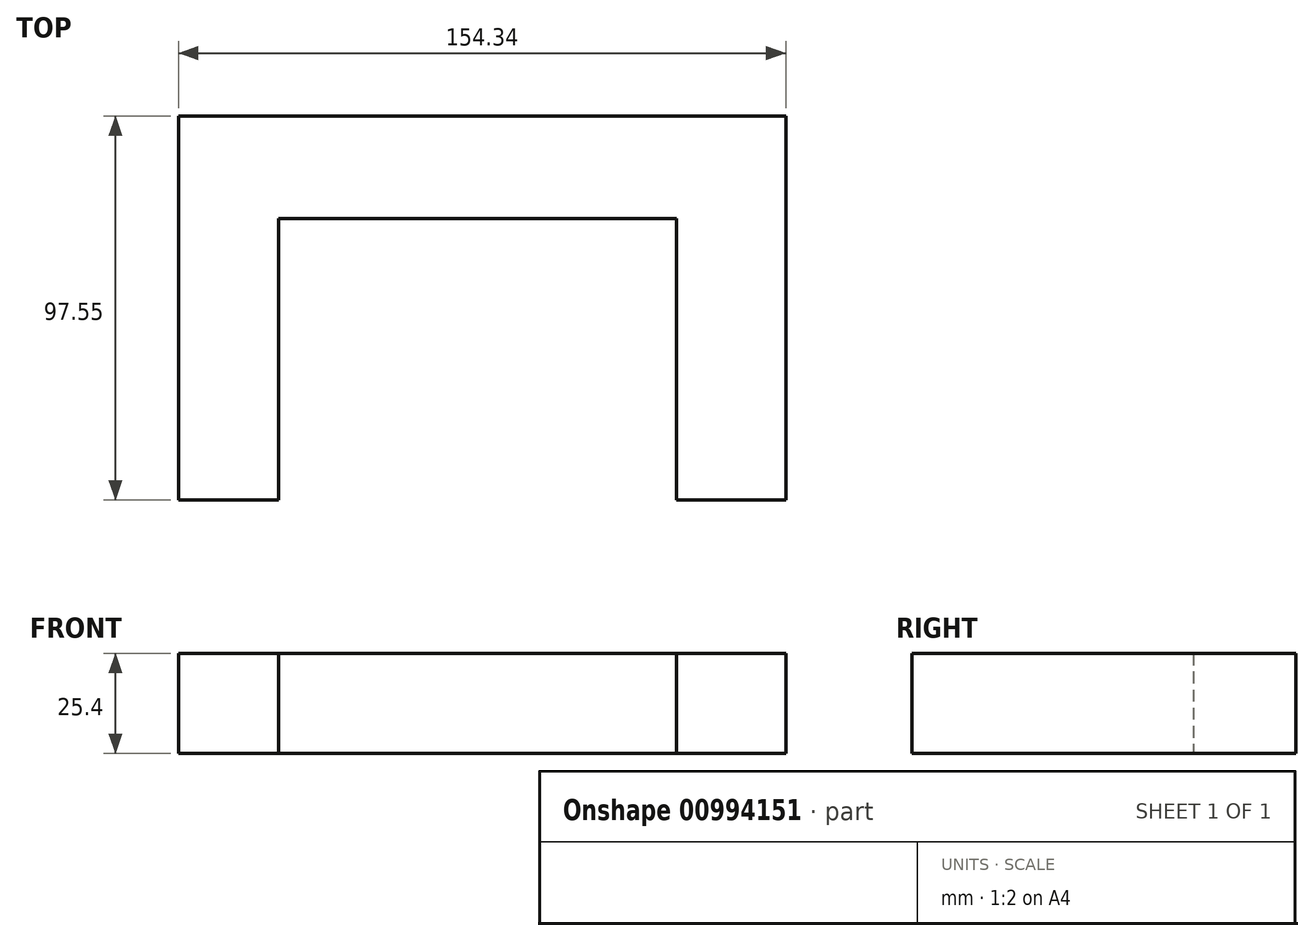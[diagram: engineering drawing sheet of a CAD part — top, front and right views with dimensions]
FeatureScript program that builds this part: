
annotation { "Feature Type Name" : "Feature", "Feature Type Description" : "" }
export const myFeature = defineFeature(function(context is Context, id is Id, definition is map)
    precondition{}
    {
        {
            var Q0;
            Q0=qCreatedBy(makeId("Top.planeOp"),FACE);
            var sketch = newSketch(context, id + "F0", { "sketchPlane" : qUnion([Q0])});
            skLineSegment(sketch, "E0.bottom", {"start": v(86.83, 58.57) * mm, "end": v(-67.5, 58.57) * mm});
            skLineSegment(sketch, "E0.top", {"start": v(86.83, -38.98) * mm, "end": v(-67.5, -38.98) * mm});
            skLineSegment(sketch, "E0.left", {"start": v(86.83, 58.57) * mm, "end": v(86.83, -38.98) * mm});
            skLineSegment(sketch, "E0.right", {"start": v(-67.5, 58.57) * mm, "end": v(-67.5, -38.98) * mm});
            skLineSegment(sketch, "E1", {"start": v(-42.07, 17.04) * mm, "end": v(-42.07, -38.98) * mm});
            skLineSegment(sketch, "E2", {"start": v(-42.07, -38.98) * mm, "end": v(-42.07, 32.56) * mm});
            skLineSegment(sketch, "E3", {"start": v(-42.07, 32.56) * mm, "end": v(59.07, 32.56) * mm});
            skLineSegment(sketch, "E4", {"start": v(59.07, 32.56) * mm, "end": v(59.07, -38.98) * mm});
            skSolve(sketch);
        }
        {
            var Q0;
            Q0=makeQuery(id+"F0.imprint","IMPRINT",FACE,{"disambiguationData":[TD([[makeQuery(id+"F0.imprint","IMPRINT",EDGE,{"derivedFrom":sQuery(id+"F0.wireOp",EDGE,"E0.bottom")}),1.0]])]});
            extrude(context, id + "F1", {"entities" : qUnion([Q0]), "depth" : 25.4 * mm, "offsetDistance" : 25.4 * mm});
        }
    });
